# Revit family: Zumtobel LITECOM CCD DALI-2
name_source: partatom
category: Lighting Fixtures
revit_build: Autodesk Revit 2016 (Build: 20150220_1215(x64)
units: mm (PartAtom-declared; Revit-internal decimal feet)

## family parameters
Cut with Voids When Loaded = Yes
Host = Face
Light Source = No
OmniClass Number = 23.80.70.11
OmniClass Title = Luminaries for Internal Lighting
Part Type = Normal
Room Calculation Point = No
Round Connector Dimension = Use Diameter
Shared = No

## types (1)
- LITECOM CCD DALI-2
    Apparent Load = 0 VA
    Assembly Code = D5020200
    Default Elevation = 0 mm  [stored 0 ft]
    Description = Central DALI-2 certified automation controller
    Height = 62 mm  [stored 0.203412 ft]
    Length = 160 mm  [stored 0.524934 ft]
    Manufacturer = Zumtobel Lighting
    Model = 22171127
    URL = www.zumtobel.com/22171127
    Width = 91 mm  [stored 0.298556 ft]

note: [stored X ft] marks values corroborated as IEEE doubles in the binary element streams (Revit-internal decimal feet)

## geometry (parser evidence)
native form markers: Blend x14, Sweep x3
no freeform markers — native parametric forms only
